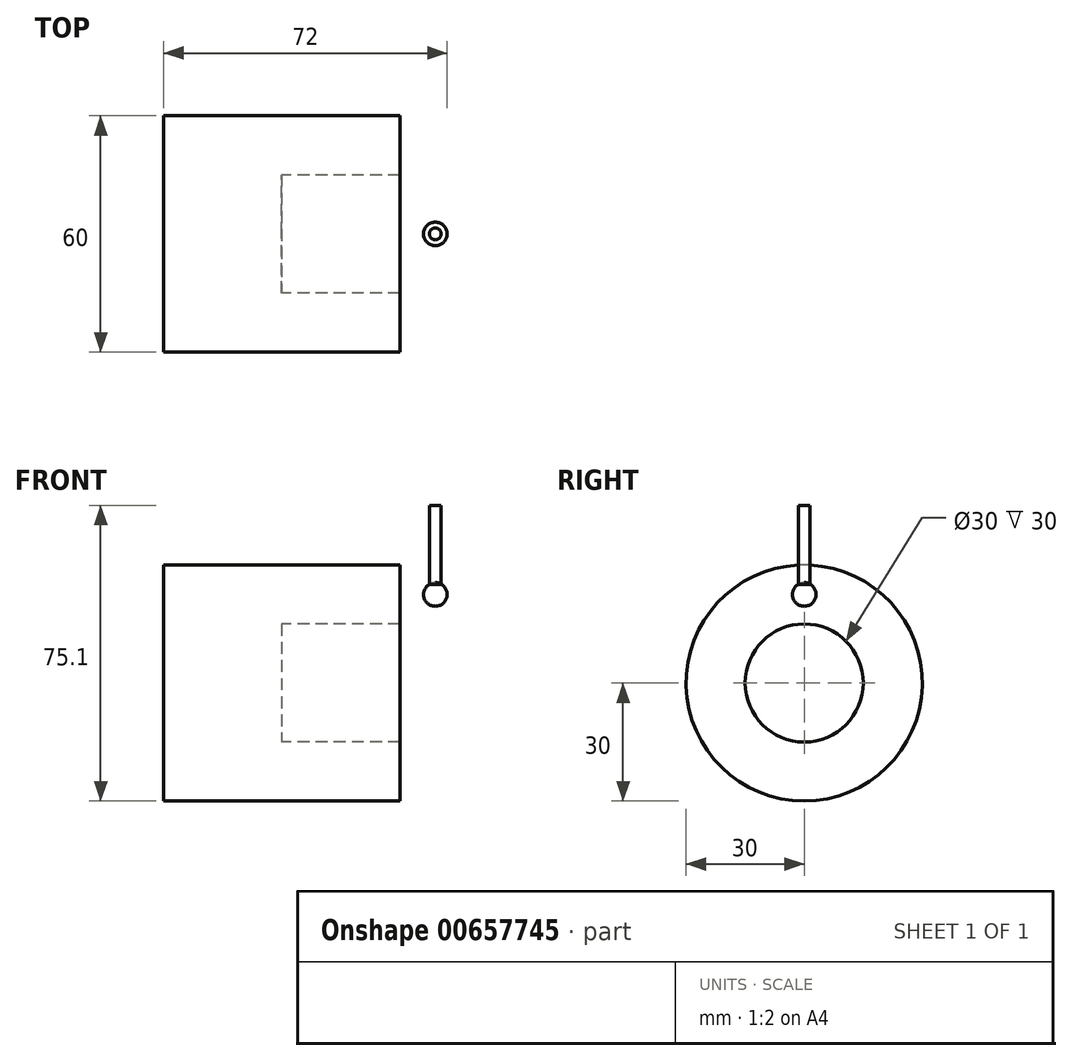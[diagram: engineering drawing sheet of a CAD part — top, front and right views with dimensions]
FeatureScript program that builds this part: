
annotation { "Feature Type Name" : "Feature", "Feature Type Description" : "" }
export const myFeature = defineFeature(function(context is Context, id is Id, definition is map)
    precondition{}
    {
        {
            var Q0;
            Q0=qCreatedBy(makeId("Front.planeOp"),FACE);
            var sketch = newSketch(context, id + "F0", { "sketchPlane" : qUnion([Q0])});
            skLineSegment(sketch, "E0.bottom", {"start": v(-60, 0) * mm, "end": v(0, 0) * mm, "construction": true});
            skLineSegment(sketch, "E0.top", {"start": v(-60, 30) * mm, "end": v(0, 30) * mm});
            skLineSegment(sketch, "E0.left", {"start": v(-60, 0) * mm, "end": v(-60, 30) * mm});
            skLineSegment(sketch, "E0.right", {"start": v(0, 15) * mm, "end": v(0, 30) * mm});
            skLineSegment(sketch, "E1", {"start": v(0, 15) * mm, "end": v(-30, 15) * mm});
            skLineSegment(sketch, "E2", {"start": v(-30, 15) * mm, "end": v(-30, 0) * mm});
            skLineSegment(sketch, "E3", {"start": v(-30, 0) * mm, "end": v(-60, 0) * mm});
            skSolve(sketch);
        }
        {
            var Q0;
            Q0 = qSketchRegion(id + "F0", true);
            var Q1;
            Q1=sQuery(id+"F0.wireOp",EDGE,"E0.bottom");
            revolve(context, id + "F1", {"surfaceOperationType" : NewSurfaceOperationType.NEW, "entities" : qUnion([Q0]), "axis" : qUnion([Q1]), "revolveType" : RevolveType.FULL});
        }
        {
            var Q0;
            Q0=qCreatedBy(makeId("Front.planeOp"),FACE);
            var sketch = newSketch(context, id + "F2", { "sketchPlane" : qUnion([Q0])});
            skArc(sketch, "E4", {"start": v(9, 25.5) * mm, "mid": v(6, 22.5) * mm, "end": v(9, 19.5) * mm});
            skLineSegment(sketch, "E5", {"start": v(9, 14.18) * mm, "end": v(9, 44.55) * mm, "construction": true});
            skLineSegment(sketch, "E6", {"start": v(9, 25.5) * mm, "end": v(9, 19.5) * mm});
            skSolve(sketch);
        }
        {
            var Q0;
            Q0 = qSketchRegion(id + "F2", true);
            var Q1;
            Q1=sQuery(id+"F2.wireOp",EDGE,"E5");
            revolve(context, id + "F3", {"surfaceOperationType" : NewSurfaceOperationType.NEW, "entities" : qUnion([Q0]), "axis" : qUnion([Q1]), "revolveType" : RevolveType.FULL});
        }
        {
            var Q0;
            Q0=qCreatedBy(makeId("Front.planeOp"),FACE);
            var sketch = newSketch(context, id + "F4", { "sketchPlane" : qUnion([Q0])});
            skLineSegment(sketch, "E7", {"start": v(9, 10.24) * mm, "end": v(9, 39.06) * mm, "construction": true});
            skArc(sketch, "E8.0", {"start": v(9, 25.5) * mm, "mid": v(8.22, 25.4) * mm, "end": v(7.5, 25.1) * mm});
            skLineSegment(sketch, "E9", {"start": v(9, 25.5) * mm, "end": v(9, 45.1) * mm});
            skLineSegment(sketch, "E10", {"start": v(9, 45.1) * mm, "end": v(7.5, 45.1) * mm});
            skLineSegment(sketch, "E11", {"start": v(7.5, 45.1) * mm, "end": v(7.5, 25.1) * mm});
            skSolve(sketch);
        }
        {
            var Q0;
            Q0 = qSketchRegion(id + "F4", true);
            var Q1;
            Q1=sQuery(id+"F4.wireOp",EDGE,"E7");
            revolve(context, id + "F5", {"surfaceOperationType" : NewSurfaceOperationType.NEW, "entities" : qUnion([Q0]), "axis" : qUnion([Q1]), "revolveType" : RevolveType.FULL});
        }
    });
